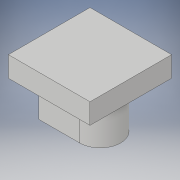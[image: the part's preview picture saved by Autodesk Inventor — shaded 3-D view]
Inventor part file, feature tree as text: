
AUTODESK INVENTOR PART (.ipt)
format: ipt  version: 2019 (Build 230136000, 136)  size: 109,056 bytes
history: native  units: mm
features: extrude x2, sketch x1
ambient origin geometry x8: Origin, YZ Plane, XZ Plane, XY Plane, X Axis, Y Axis, Z Axis, Center Point
bodies: Solid1 (feature_tree)
feature tree (3):
  sketch  "Sketch1"  dims[d0=20.0mm d1=20.0mm d2=2.5mm d3=2.5mm d4=2.5mm d5=2.5mm d6=5.0mm d7=10.0mm d8=0.0mm d9=5.0mm d10=0.0mm]
  extrude  "Extrusion1"  Depth=20.0mm
  extrude  "Extrusion2"  Depth=2.5mm
